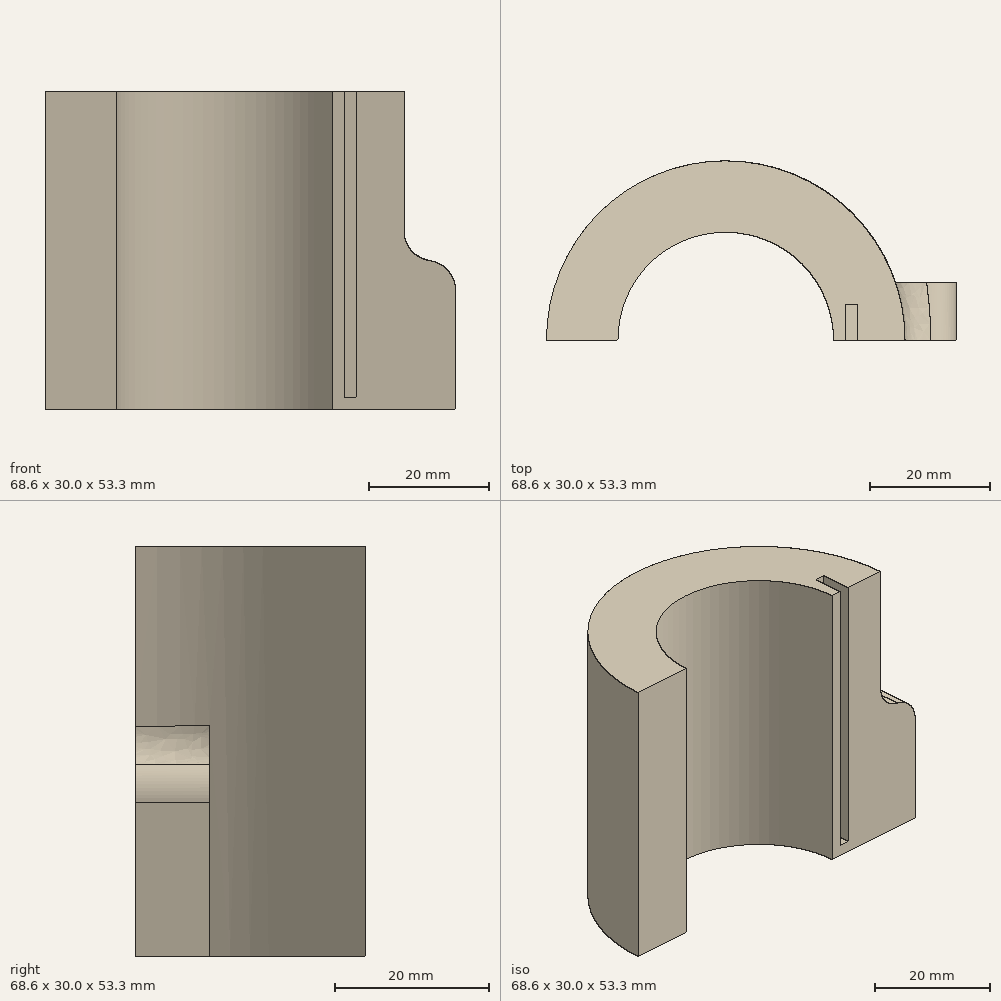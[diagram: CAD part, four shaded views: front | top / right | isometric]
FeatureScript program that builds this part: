
annotation { "Feature Type Name" : "Feature", "Feature Type Description" : "" }
export const myFeature = defineFeature(function(context is Context, id is Id, definition is map)
    precondition{}
    {
        {
            var Q0;
            Q0=qCreatedBy(makeId("Front.planeOp"),FACE);
            var sketch = newSketch(context, id + "F0", { "sketchPlane" : qUnion([Q0])});
            skLineSegment(sketch, "E0.bottom", {"start": v(-18.04, 0) * mm, "end": v(-30, 0) * mm});
            skLineSegment(sketch, "E0.top", {"start": v(-18.04, 53.3) * mm, "end": v(-30, 53.3) * mm});
            skLineSegment(sketch, "E0.left", {"start": v(-18.04, 0) * mm, "end": v(-18.04, 53.3) * mm});
            skLineSegment(sketch, "E0.right", {"start": v(-30, 0) * mm, "end": v(-30, 53.3) * mm});
            skLineSegment(sketch, "E1", {"start": v(0, 0) * mm, "end": v(0, 60.54) * mm});
            skSolve(sketch);
        }
        {
            var Q0;
            Q0=makeQuery(id+"F0.imprint","IMPRINT",FACE,{"disambiguationData":[TD([[makeQuery(id+"F0.imprint","IMPRINT",EDGE,{"derivedFrom":sQuery(id+"F0.wireOp",EDGE,"E0.bottom")}),-1.0]])]});
            var Q1;
            Q1=sQuery(id+"F0.wireOp",EDGE,"E1");
            revolve(context, id + "F1", {"surfaceOperationType" : NewSurfaceOperationType.NEW, "entities" : qUnion([Q0]), "axis" : qUnion([Q1]), "revolveType" : RevolveType.FULL});
        }
        {
            var Q0;
            Q0=makeQuery(id+"F1.opRevolve","SWEPT_FACE",FACE,{"disambiguationData":[OSD([sQuery(id+"F0.wireOp",EDGE,"E0.bottom")])]});
            var sketch = newSketch(context, id + "F2", { "sketchPlane" : qUnion([Q0])});
            skSolve(sketch);
        }
        {
            var Q0;
            Q0=makeQuery(id+"FB7IoJT8i0enXo5_1.boolean.opBoolean","MERGE",FACE,{"derivedFrom":[makeQuery(id+"F1.opRevolve","SWEPT_FACE",FACE,{"disambiguationData":[OSD([sQuery(id+"F0.wireOp",EDGE,"E0.bottom")])]}),makeQuery(id+"FB7IoJT8i0enXo5_1.opExtrude","CAP_FACE",FACE,{"disambiguationData":[OSD([sQuery(id+"F2.wireOp",EDGE,"Kp4PaSQW-HKNf-P2XU-XyM2-LQGMbnZUrEG6.bottom"),sQuery(id+"F2.wireOp",EDGE,"Kp4PaSQW-HKNf-P2XU-XyM2-LQGMbnZUrEG6.top"),sQuery(id+"F2.wireOp",EDGE,"Kp4PaSQW-HKNf-P2XU-XyM2-LQGMbnZUrEG6.left"),sQuery(id+"F2.wireOp",EDGE,"Kp4PaSQW-HKNf-P2XU-XyM2-LQGMbnZUrEG6.right")])],"isStart":true})]});
            var sketch = newSketch(context, id + "F3", { "sketchPlane" : qUnion([Q0])});
            skLineSegment(sketch, "E2.bottom", {"start": v(-53.15, 0) * mm, "end": v(50.54, 0) * mm});
            skLineSegment(sketch, "E2.top", {"start": v(-53.15, 58.88) * mm, "end": v(50.54, 58.88) * mm});
            skLineSegment(sketch, "E2.left", {"start": v(-53.15, 0) * mm, "end": v(-53.15, 58.88) * mm});
            skLineSegment(sketch, "E2.right", {"start": v(50.54, 0) * mm, "end": v(50.54, 58.88) * mm});
            skSolve(sketch);
        }
        {
            var Q0;
            Q0=qSketchRegion(id+"F3",true);
            extrude(context, id + "F4", {"entities" : qUnion([Q0]), "operationType" : NewBodyOperationType.REMOVE, "endBound" : BoundingType.THROUGH_ALL, "oppositeDirection" : true, "depth" : 25 * mm, "offsetDistance" : 25 * mm});
        }
        {
            var Q0;
            Q0=qCreatedBy(makeId("Top.planeOp"),FACE);
            var sketch = newSketch(context, id + "F5", { "sketchPlane" : qUnion([Q0])});
            skLineSegment(sketch, "E3.bottom", {"start": v(26.99, 9.69) * mm, "end": v(38.61, 9.69) * mm});
            skLineSegment(sketch, "E3.top", {"start": v(26.99, -9.69) * mm, "end": v(38.61, -9.69) * mm});
            skLineSegment(sketch, "E3.left", {"start": v(26.99, 9.69) * mm, "end": v(26.99, -9.69) * mm});
            skLineSegment(sketch, "E3.right", {"start": v(38.61, 9.69) * mm, "end": v(38.61, -9.69) * mm});
            skPoint(sketch, "E3.middle", {"position": v(32.8, 0) * mm});
            skSolve(sketch);
        }
        {
            var Q0;
            Q0=makeQuery(id+"F5.imprint","IMPRINT",FACE,{"disambiguationData":[TD([[makeQuery(id+"F5.imprint","IMPRINT",EDGE,{"derivedFrom":sQuery(id+"F5.wireOp",EDGE,"E3.bottom")}),-1.0]])]});
            extrude(context, id + "F6", {"entities" : qUnion([Q0]), "operationType" : NewBodyOperationType.ADD, "depth" : 25 * mm, "offsetDistance" : 25 * mm});
        }
        {
            var Q0;
            Q0=qCreatedBy(makeId("Right.planeOp"),FACE);
            var sketch = newSketch(context, id + "F7", { "sketchPlane" : qUnion([Q0])});
            skLineSegment(sketch, "E4.bottom", {"start": v(0, -6.37) * mm, "end": v(-71.7, -6.37) * mm});
            skLineSegment(sketch, "E4.top", {"start": v(0, 110.44) * mm, "end": v(-71.7, 110.44) * mm});
            skLineSegment(sketch, "E4.left", {"start": v(0, -6.37) * mm, "end": v(0, 110.44) * mm});
            skLineSegment(sketch, "E4.right", {"start": v(-71.7, -6.37) * mm, "end": v(-71.7, 110.44) * mm});
            skPoint(sketch, "E4.middle", {"position": v(-35.85, 52.04) * mm});
            skSolve(sketch);
        }
        {
            var Q0;
            Q0=makeQuery(id+"F7.imprint","IMPRINT",FACE,{"disambiguationData":[TD([[makeQuery(id+"F7.imprint","IMPRINT",EDGE,{"derivedFrom":sQuery(id+"F7.wireOp",EDGE,"E4.bottom")}),-1.0]])]});
            extrude(context, id + "F8", {"entities" : qUnion([Q0]), "operationType" : NewBodyOperationType.REMOVE, "endBound" : BoundingType.THROUGH_ALL, "depth" : 25 * mm, "offsetDistance" : 25 * mm});
        }
        {
            var Q0;
            Q0=qCreatedBy(makeId("Front.planeOp"),FACE);
            var sketch = newSketch(context, id + "F9", { "sketchPlane" : qUnion([Q0])});
            skLineSegment(sketch, "E5.bottom", {"start": v(20.04, 53.3) * mm, "end": v(22.04, 53.3) * mm});
            skLineSegment(sketch, "E5.top", {"start": v(20.04, 2) * mm, "end": v(22.04, 2) * mm});
            skLineSegment(sketch, "E5.left", {"start": v(20.04, 53.3) * mm, "end": v(20.04, 2) * mm});
            skLineSegment(sketch, "E5.right", {"start": v(22.04, 53.3) * mm, "end": v(22.04, 2) * mm});
            skSolve(sketch);
        }
        {
            var Q0;
            Q0=makeQuery(id+"F9.imprint","IMPRINT",FACE,{"disambiguationData":[TD([[makeQuery(id+"F9.imprint","IMPRINT",EDGE,{"derivedFrom":sQuery(id+"F9.wireOp",EDGE,"E5.bottom")}),-1.0]])]});
            extrude(context, id + "F10", {"entities" : qUnion([Q0]), "operationType" : NewBodyOperationType.REMOVE, "oppositeDirection" : true, "depth" : 6 * mm, "offsetDistance" : 25 * mm});
        }
        {
            var Q0;
            Q0=makeQuery(id+"F6.opExtrude","CAP_EDGE",EDGE,{"disambiguationData":[OSD([sQuery(id+"F5.wireOp",EDGE,"E3.right")])],"isStart":false});
            fillet(context, id + "F11", {"entities" : qUnion([Q0]), "radius" : 5 * mm, "tangentPropagation" : true, "allowEdgeOverflow" : false});
        }
        {
            var Q0;
            Q0=makeQuery(id+"F6.boolean.opBoolean","INTERSECT",EDGE,{"derivedFrom":[makeQuery(id+"F1.opRevolve","SWEPT_FACE",FACE,{"disambiguationData":[OSD([sQuery(id+"F0.wireOp",EDGE,"E0.right")])]}),makeQuery(id+"F6.opExtrude","CAP_FACE",FACE,{"disambiguationData":[OSD([sQuery(id+"F5.wireOp",EDGE,"E3.bottom"),sQuery(id+"F5.wireOp",EDGE,"E3.top"),sQuery(id+"F5.wireOp",EDGE,"E3.left"),sQuery(id+"F5.wireOp",EDGE,"E3.right")])],"isStart":false})]});
            fillet(context, id + "F12", {"entities" : qUnion([Q0]), "radius" : 5 * mm, "tangentPropagation" : true, "allowEdgeOverflow" : false});
        }
    });
